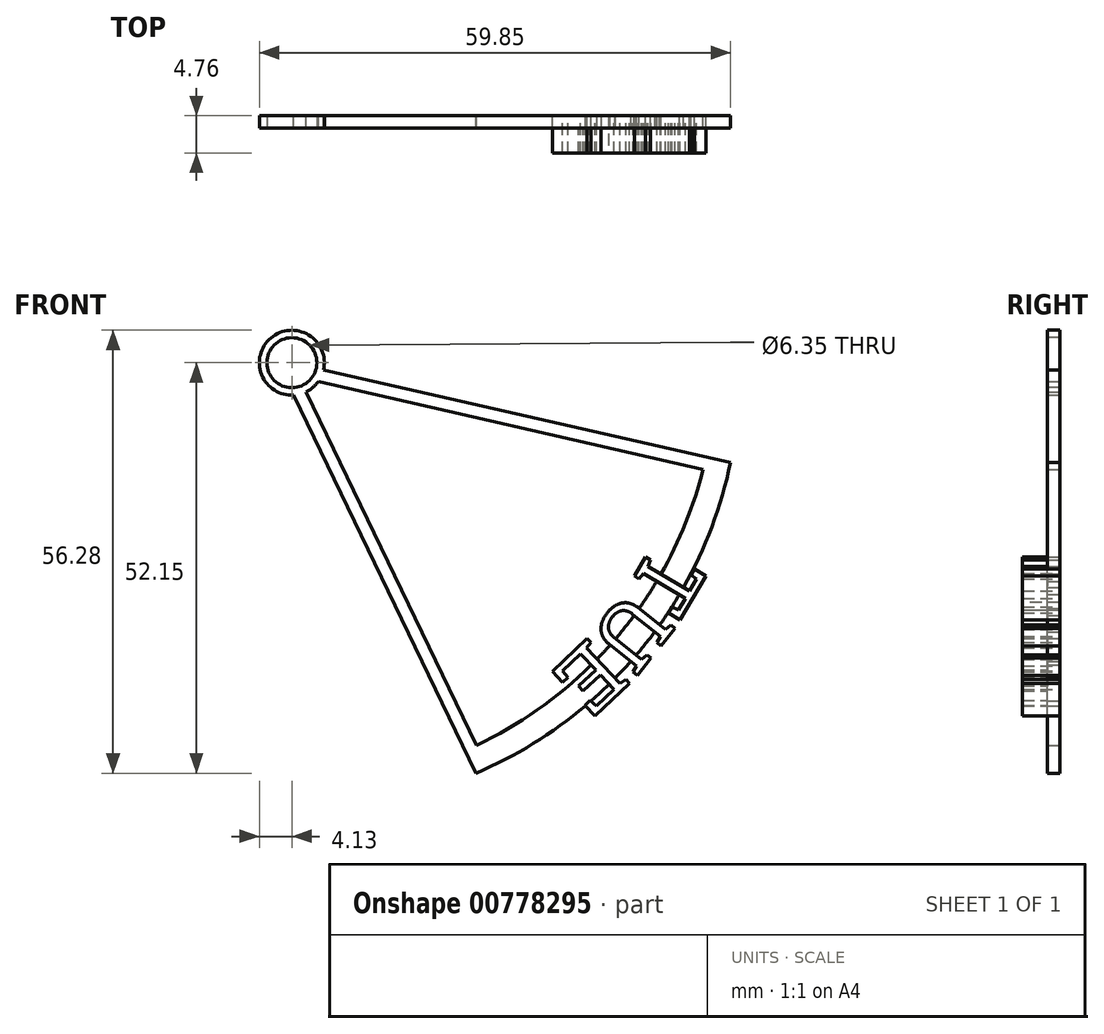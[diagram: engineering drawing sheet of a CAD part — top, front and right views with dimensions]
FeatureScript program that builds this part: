
annotation { "Feature Type Name" : "Feature", "Feature Type Description" : "" }
export const myFeature = defineFeature(function(context is Context, id is Id, definition is map)
    precondition{}
    {
        {
            var Q0;
            Q0=qCreatedBy(makeId("Front.planeOp"),FACE);
            var sketch = newSketch(context, id + "F0", { "sketchPlane" : qUnion([Q0])});
            skCircle(sketch, "E0", {"center": v(0, 0) * mm, "radius": 59.18 * mm, "construction": true});
            skCircle(sketch, "E1", {"center": v(0, 0) * mm, "radius": 50.8 * mm, "construction": true});
            skLineSegment(sketch, "E2", {"start": v(0, 0) * mm, "end": v(0, 59.18) * mm, "construction": true});
            skLineSegment(sketch, "E3", {"start": v(0, 0) * mm, "end": v(57.7, -13.15) * mm, "construction": true});
            skLineSegment(sketch, "E4", {"start": v(0, 0) * mm, "end": v(50.93, -30.14) * mm, "construction": true});
            skLineSegment(sketch, "E5", {"start": v(0, 0) * mm, "end": v(46.24, -36.93) * mm, "construction": true});
            skLineSegment(sketch, "E6", {"start": v(0, 0) * mm, "end": v(40.65, -43) * mm, "construction": true});
            skText(sketch, "E7", { "text": "T", "fontName": "RobotoSlab-Regular.ttf"});
            skText(sketch, "E8", { "text": "U", "fontName": "RobotoSlab-Regular.ttf"});
            skText(sketch, "E9", { "text": "E", "fontName": "RobotoSlab-Regular.ttf"});
            skLineSegment(sketch, "E10", {"start": v(0, 0) * mm, "end": v(52.82, -26.95) * mm, "construction": true});
            skLineSegment(sketch, "E11", {"start": v(0, 0) * mm, "end": v(38.06, -45.46) * mm, "construction": true});
            skLineSegment(sketch, "E12", {"start": v(0, 0) * mm, "end": v(25.7, -53.3) * mm, "construction": true});
            const initialGuessF0  = {"E7": [0.04599, -0.02291, -0.50921, -0.86064, 0.00794], "E8": [0.04274, -0.0286, -0.62403, -0.7814, 0.00794], "E9": [0.0378, -0.03479, -0.72671, -0.68694, 0.00794]};
            skSetInitialGuess(sketch, initialGuessF0);
            skSolve(sketch);
        }
        {
            var Q0;
            Q0=qSketchRegion(id+"F0",true);
            extrude(context, id + "F1", {"entities" : qUnion([Q0]), "depth" : 4.76 * mm, "offsetDistance" : 25.4 * mm});
        }
        {
            var Q0;
            Q0=qCreatedBy(makeId("Front.planeOp"),FACE);
            var sketch = newSketch(context, id + "F2", { "sketchPlane" : qUnion([Q0])});
            skCircle(sketch, "E13", {"center": v(0, 0) * mm, "radius": 4.13 * mm, "construction": true});
            skCircle(sketch, "E14", {"center": v(0, 0) * mm, "radius": 53.98 * mm, "construction": true});
            skCircle(sketch, "E15", {"center": v(0, 0) * mm, "radius": 57.15 * mm, "construction": true});
            skLineSegment(sketch, "E16", {"start": v(0, 0) * mm, "end": v(0, 57.15) * mm, "construction": true});
            skLineSegment(sketch, "E17", {"start": v(0, 0) * mm, "end": v(55.72, -12.7) * mm, "construction": true});
            skLineSegment(sketch, "E18", {"start": v(52.25, -13.54) * mm, "end": v(3.36, -2.4) * mm, "construction": true});
            skLineSegment(sketch, "E19", {"start": v(23.44, -48.62) * mm, "end": v(0, 0) * mm, "construction": true});
            skLineSegment(sketch, "E20", {"start": v(23.38, -52.15) * mm, "end": v(0.22, -4.12) * mm, "construction": true});
            skLineSegment(sketch, "E21", {"start": v(3.36, -2.4) * mm, "end": v(52.25, -13.54) * mm});
            skLineSegment(sketch, "E22", {"start": v(23.44, -48.62) * mm, "end": v(1.8, -3.72) * mm});
            skLineSegment(sketch, "E23", {"start": v(23.38, -52.15) * mm, "end": v(0.22, -4.12) * mm});
            skLineSegment(sketch, "E24", {"start": v(55.72, -12.7) * mm, "end": v(4.02, -0.92) * mm});
            skCircle(sketch, "E25", {"center": v(0, 0) * mm, "radius": 4.13 * mm});
            skArc(sketch, "E26", {"start": v(23.44, -48.62) * mm, "mid": v(41.76, -34.3) * mm, "end": v(52.25, -13.54) * mm});
            skArc(sketch, "E27", {"start": v(23.38, -52.15) * mm, "mid": v(44.38, -36.39) * mm, "end": v(55.72, -12.7) * mm});
            skSolve(sketch);
        }
        {
            var Q0;
            {var subQ0=sQuery(id+"F2.wireOp",EDGE,"E25");var subQ1=makeQuery(id+"F2.imprint","INTERSECT",VERTEX,{"derivedFrom":[sQuery(id+"F2.wireOp",EDGE,"E22"),subQ0]});Q0=makeQuery(id+"F2.imprint","IMPRINT",FACE,{"disambiguationData":[TD([[makeQuery(id+"F2.imprint","IMPRINT",EDGE,{"disambiguationData":[TD([[subQ1,1.0]])],"derivedFrom":subQ0}),1.0]])]});}
            var Q1;
            {var subQ3=sQuery(id+"F2.wireOp",EDGE,"E21");Q1=makeQuery(id+"F2.imprint","IMPRINT",FACE,{"disambiguationData":[TD([[makeQuery(id+"F2.imprint","IMPRINT",EDGE,{"derivedFrom":subQ3}),1.0]])]});}
            extrude(context, id + "F3", {"entities" : qUnion([Q0, Q1]), "operationType" : NewBodyOperationType.ADD, "depth" : 1.59 * mm, "offsetDistance" : 25.4 * mm});
        }
        {
            var Q0;
            {var subQ0=sQuery(id+"F2.wireOp",EDGE,"E26");var subQ1=sQuery(id+"F2.wireOp",EDGE,"E25");var subQ2=sQuery(id+"F2.wireOp",EDGE,"E23");var subQ3=sQuery(id+"F2.wireOp",EDGE,"E24");var subQ4=sQuery(id+"F2.wireOp",EDGE,"E21");var subQ5=sQuery(id+"F2.wireOp",EDGE,"E22");var subQ6=sQuery(id+"F2.wireOp",EDGE,"E27");Q0=makeQuery(id+"F3.boolean.opBoolean","SPLIT",FACE,{"disambiguationData":[TD([makeQuery(id+"F1.opExtrude","SWEPT_FACE",FACE,{"disambiguationData":[OSD([sQuery(id+"F0.wireOp",EDGE,"E7.sketch_text.stroke-10")])]})])],"derivedFrom":makeQuery(id+"F3.opExtrude","CAP_FACE",FACE,{"disambiguationData":[OSD([subQ4,subQ5,subQ2,subQ3,subQ1,subQ0,subQ6])],"isStart":false})});}
            var sketch = newSketch(context, id + "F4", { "sketchPlane" : qUnion([Q0])});
            skPoint(sketch, "E28", {"position": v(0, 0) * mm});
            skSolve(sketch);
        }
        {
            var Q0;
            Q0=sQuery(id+"F4.wireOp",VERTEX,"E28");
            var Q1;
            Q1=makeQuery(id+"F1.opExtrude","SWEPT_BODY",BODY,{"disambiguationData":[OSD([sQuery(id+"F0.wireOp",EDGE,"E7.sketch_text.stroke-0"),sQuery(id+"F0.wireOp",EDGE,"E7.sketch_text.stroke-1"),sQuery(id+"F0.wireOp",EDGE,"E7.sketch_text.stroke-2"),sQuery(id+"F0.wireOp",EDGE,"E7.sketch_text.stroke-3"),sQuery(id+"F0.wireOp",EDGE,"E7.sketch_text.stroke-4"),sQuery(id+"F0.wireOp",EDGE,"E7.sketch_text.stroke-5"),sQuery(id+"F0.wireOp",EDGE,"E7.sketch_text.stroke-6"),sQuery(id+"F0.wireOp",EDGE,"E7.sketch_text.stroke-7"),sQuery(id+"F0.wireOp",EDGE,"E7.sketch_text.stroke-8"),sQuery(id+"F0.wireOp",EDGE,"E7.sketch_text.stroke-9"),sQuery(id+"F0.wireOp",EDGE,"E7.sketch_text.stroke-10"),sQuery(id+"F0.wireOp",EDGE,"E7.sketch_text.stroke-11"),sQuery(id+"F0.wireOp",EDGE,"E7.sketch_text.stroke-12"),sQuery(id+"F0.wireOp",EDGE,"E7.sketch_text.stroke-13"),sQuery(id+"F0.wireOp",EDGE,"E7.sketch_text.stroke-14"),sQuery(id+"F0.wireOp",EDGE,"E7.sketch_text.stroke-15")])]});
            hole(context, id + "F5", {"style" : HoleStyle.SIMPLE, "endStyle" : HoleEndStyle.THROUGH, "holeDiameter" : 6.35 * mm, "majorDiameter" : 6.35 * mm, "isTappedThrough" : true, "tappedDepth" : 12.7 * mm, "tapClearance" : 3, "locations" : qUnion([Q0]), "scope" : qUnion([Q1])});
        }
    });
